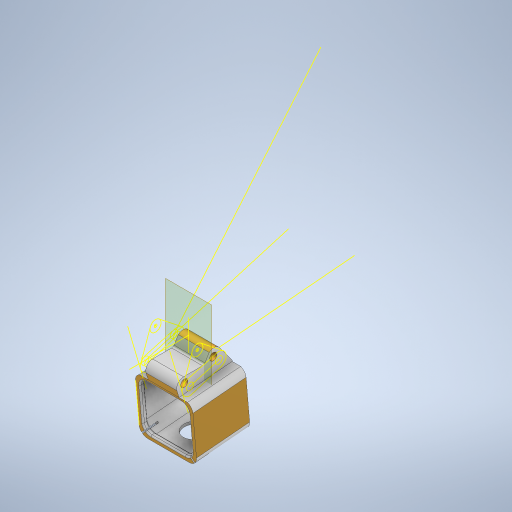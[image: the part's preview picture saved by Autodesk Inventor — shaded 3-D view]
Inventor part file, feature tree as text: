
AUTODESK INVENTOR PART (.ipt)
format: ipt  version: 2023 (Build 270158000, 158)  size: 855,552 bytes
history: native  units: in
note: dims shown in document units (in); Inventor stores cm internally (conversion verified against a paired STEP export)
features: sketch x10, projected_geometry x6, extrude x5, other x3, fillet x2, plane x1
ambient origin geometry x8: Origin, YZ Plane, XZ Plane, XY Plane, X Axis, Y Axis, Z Axis, Center Point
bodies: Solid1 (feature_tree)
feature tree (27):
  other  "45 deg with session mount for boolian.iam"
  other  "45 deg mini predator fixed mount.ipt:1"
  other  "V2 session mount 45deg block.ipt:1"
  extrude  "Extrusion1"  Depth=0.3937in TaperAngle=0.0deg
  extrude  "Extrusion2"  Depth=0.0906in
  extrude  "Extrusion3"  Depth=0.3937in TaperAngle=0.0deg
  extrude  "Extrusion4"  Depth=0.3937in TaperAngle=0.0deg
  extrude  "Extrusion5"  Depth=0.0787in
  fillet  "Fillet1"  [1 undecoded]
  fillet  "Fillet2"  [1 undecoded]
  sketch  "Sketch18"
  sketch  "Sketch2"  dims[d3=1.0in d4=0.0in d6=0.0906in]
  sketch  "Sketch2_1"  dims[d0=0.3937in d1=1.0in d2=0.0in]
  plane  "Work Plane1"
  sketch  "Sketch6"  dims[d7=0.0906in d8=0.3937in d9=0.0in]
  sketch  "Sketch7"  dims[d10=0.3937in d11=0.0in d12=0.3937in d13=0.0in]
  sketch  "Sketch8"  dims[d14=0.1969in d15=0.0787in]
  projected_geometry  "Projected Loop1"
  sketch  "Sketch9"
  projected_geometry  "Projected Loop2"
  sketch  "Sketch10"
  projected_geometry  "Projected Loop3"
  projected_geometry  "Projected Loop4"
  projected_geometry  "Projected Loop5"
  sketch  "Sketch11"
  projected_geometry  "Projected Loop6"
  sketch  "Sketch12"
note: 2 required parameter values undecoded (feature->parameter linkage not recoverable at this tier; creation-order binding heuristic only, values carry confidence <= 0.55)
